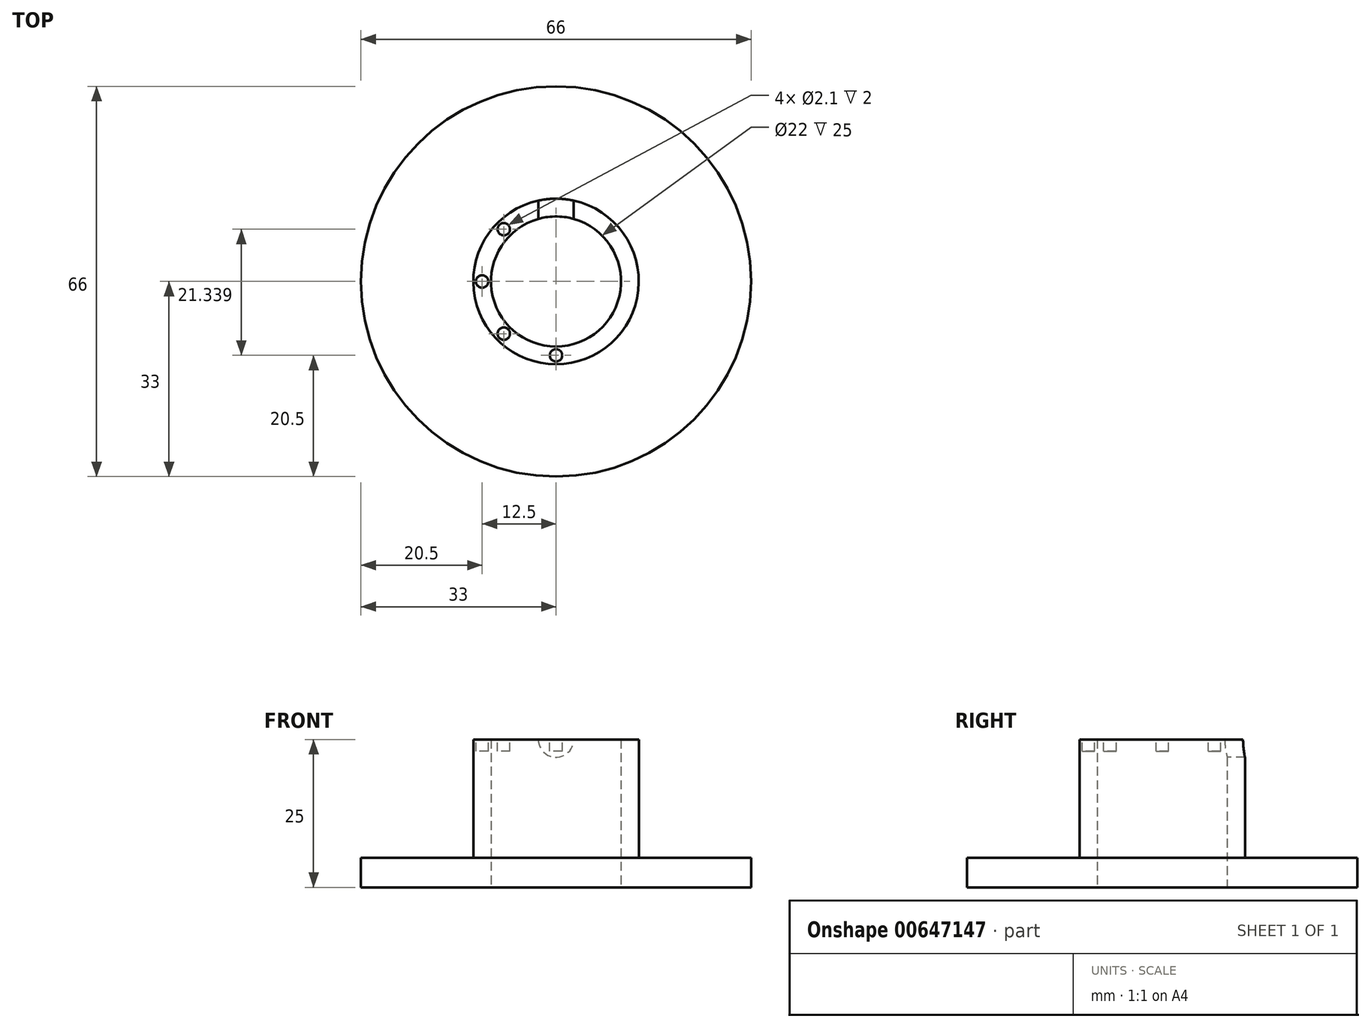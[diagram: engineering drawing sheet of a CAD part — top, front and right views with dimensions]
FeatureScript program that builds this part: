
annotation { "Feature Type Name" : "Feature", "Feature Type Description" : "" }
export const myFeature = defineFeature(function(context is Context, id is Id, definition is map)
    precondition{}
    {
        {
            var Q0;
            Q0=qCreatedBy(makeId("Top.planeOp"),FACE);
            var sketch = newSketch(context, id + "F0", { "sketchPlane" : qUnion([Q0])});
            skCircle(sketch, "E0", {"center": v(0, 0) * mm, "radius": 11 * mm});
            skCircle(sketch, "E1", {"center": v(0, 0) * mm, "radius": 33 * mm});
            skCircle(sketch, "E2.0", {"center": v(0, 0) * mm, "radius": 14 * mm});
            skSolve(sketch);
        }
        {
            var Q0;
            Q0=makeQuery(id+"F0.imprint","IMPRINT",FACE,{"disambiguationData":[TD([[makeQuery(id+"F0.imprint","IMPRINT",EDGE,{"derivedFrom":sQuery(id+"F0.wireOp",EDGE,"E0")}),-1.0]])]});
            extrude(context, id + "F1", {"entities" : qUnion([Q0]), "depth" : 25 * mm, "offsetDistance" : 25 * mm});
        }
        {
            var Q0;
            Q0=makeQuery(id+"F0.imprint","IMPRINT",FACE,{"disambiguationData":[TD([[makeQuery(id+"F0.imprint","IMPRINT",EDGE,{"derivedFrom":sQuery(id+"F0.wireOp",EDGE,"E1")}),1.0]])]});
            extrude(context, id + "F2", {"entities" : qUnion([Q0]), "operationType" : NewBodyOperationType.ADD, "depth" : 5 * mm, "offsetDistance" : 25 * mm});
        }
        {
            var Q0;
            Q0=qCreatedBy(makeId("Front.planeOp"),FACE);
            var sketch = newSketch(context, id + "F3", { "sketchPlane" : qUnion([Q0])});
            skCircle(sketch, "E3", {"center": v(0, 25) * mm, "radius": 3 * mm});
            skSolve(sketch);
        }
        {
            var Q0;
            Q0=makeQuery(id+"F3.imprint","IMPRINT",FACE,{"disambiguationData":[TD([[makeQuery(id+"F3.imprint","IMPRINT",EDGE,{"derivedFrom":sQuery(id+"F3.wireOp",EDGE,"E3")}),1.0]])]});
            extrude(context, id + "F4", {"entities" : qUnion([Q0]), "operationType" : NewBodyOperationType.REMOVE, "oppositeDirection" : true, "depth" : 25 * mm, "offsetDistance" : 25 * mm});
        }
        {
            var Q0;
            Q0=makeQuery(id+"F1.opExtrude","CAP_FACE",FACE,{"disambiguationData":[OSD([sQuery(id+"F0.wireOp",EDGE,"E0"),sQuery(id+"F0.wireOp",EDGE,"E2.0")])],"isStart":false});
            cPlane(context, id + "F5", {"entities" : qUnion([Q0]), "cplaneType" : CPlaneType.OFFSET, "offset" : 0 * mm, "width" : 150 * mm, "height" : 150 * mm});
        }
        {
            var Q0;
            Q0=qCreatedBy(id+"F5.planeOp",FACE);
            var sketch = newSketch(context, id + "F6", { "sketchPlane" : qUnion([Q0])});
            skCircle(sketch, "E4", {"center": v(0, -12.5) * mm, "radius": 1.05 * mm});
            skCircle(sketch, "E5.1.0", {"center": v(-8.84, -8.84) * mm, "radius": 1.05 * mm});
            skCircle(sketch, "E5.2.0", {"center": v(-12.5, 0) * mm, "radius": 1.05 * mm});
            skCircle(sketch, "E5.3.0", {"center": v(-8.84, 8.84) * mm, "radius": 1.05 * mm});
            skPoint(sketch, "E5.center", {"position": v(0, 0) * mm});
            skLineSegment(sketch, "E5.anchor1", {"start": v(0, 0) * mm, "end": v(0, -12.5) * mm, "construction": true});
            skLineSegment(sketch, "E5.anchor2", {"start": v(0, 0) * mm, "end": v(0, 12.5) * mm, "construction": true});
            skCircle(sketch, "E6.MirrorC", {"center": v(8.84, 8.84) * mm, "radius": 1.05 * mm});
            skCircle(sketch, "E7.MirrorC", {"center": v(12.5, 0) * mm, "radius": 1.05 * mm});
            skCircle(sketch, "E8.MirrorC", {"center": v(8.84, -8.84) * mm, "radius": 1.05 * mm});
            skSolve(sketch);
        }
        {
            var Q0;
            Q0=makeQuery(id+"F6.imprint","IMPRINT",FACE,{"disambiguationData":[TD([[makeQuery(id+"F6.imprint","IMPRINT",EDGE,{"derivedFrom":sQuery(id+"F6.wireOp",EDGE,"E5.3.0")}),1.0]])]});
            var Q1;
            Q1=makeQuery(id+"F6.imprint","IMPRINT",FACE,{"disambiguationData":[TD([[makeQuery(id+"F6.imprint","IMPRINT",EDGE,{"derivedFrom":sQuery(id+"F6.wireOp",EDGE,"E6.MirrorC")}),-1.0]])]});
            var Q2;
            Q2=makeQuery(id+"F6.imprint","IMPRINT",FACE,{"disambiguationData":[TD([[makeQuery(id+"F6.imprint","IMPRINT",EDGE,{"derivedFrom":sQuery(id+"F6.wireOp",EDGE,"E7.MirrorC")}),-1.0]])]});
            var Q3;
            Q3=makeQuery(id+"F6.imprint","IMPRINT",FACE,{"disambiguationData":[TD([[makeQuery(id+"F6.imprint","IMPRINT",EDGE,{"derivedFrom":sQuery(id+"F6.wireOp",EDGE,"E8.MirrorC")}),-1.0]])]});
            var Q4;
            Q4=makeQuery(id+"F6.imprint","IMPRINT",FACE,{"disambiguationData":[TD([[makeQuery(id+"F6.imprint","IMPRINT",EDGE,{"derivedFrom":sQuery(id+"F6.wireOp",EDGE,"E4")}),1.0]])]});
            var Q5;
            Q5=makeQuery(id+"F6.imprint","IMPRINT",FACE,{"disambiguationData":[TD([[makeQuery(id+"F6.imprint","IMPRINT",EDGE,{"derivedFrom":sQuery(id+"F6.wireOp",EDGE,"E5.1.0")}),1.0]])]});
            var Q6;
            Q6=makeQuery(id+"F6.imprint","IMPRINT",FACE,{"disambiguationData":[TD([[makeQuery(id+"F6.imprint","IMPRINT",EDGE,{"derivedFrom":sQuery(id+"F6.wireOp",EDGE,"E5.2.0")}),1.0]])]});
            extrude(context, id + "F7", {"entities" : qUnion([Q0, Q1, Q2, Q3, Q4, Q5, Q6]), "operationType" : NewBodyOperationType.REMOVE, "oppositeDirection" : true, "depth" : 2 * mm, "offsetDistance" : 25 * mm});
        }
    });
